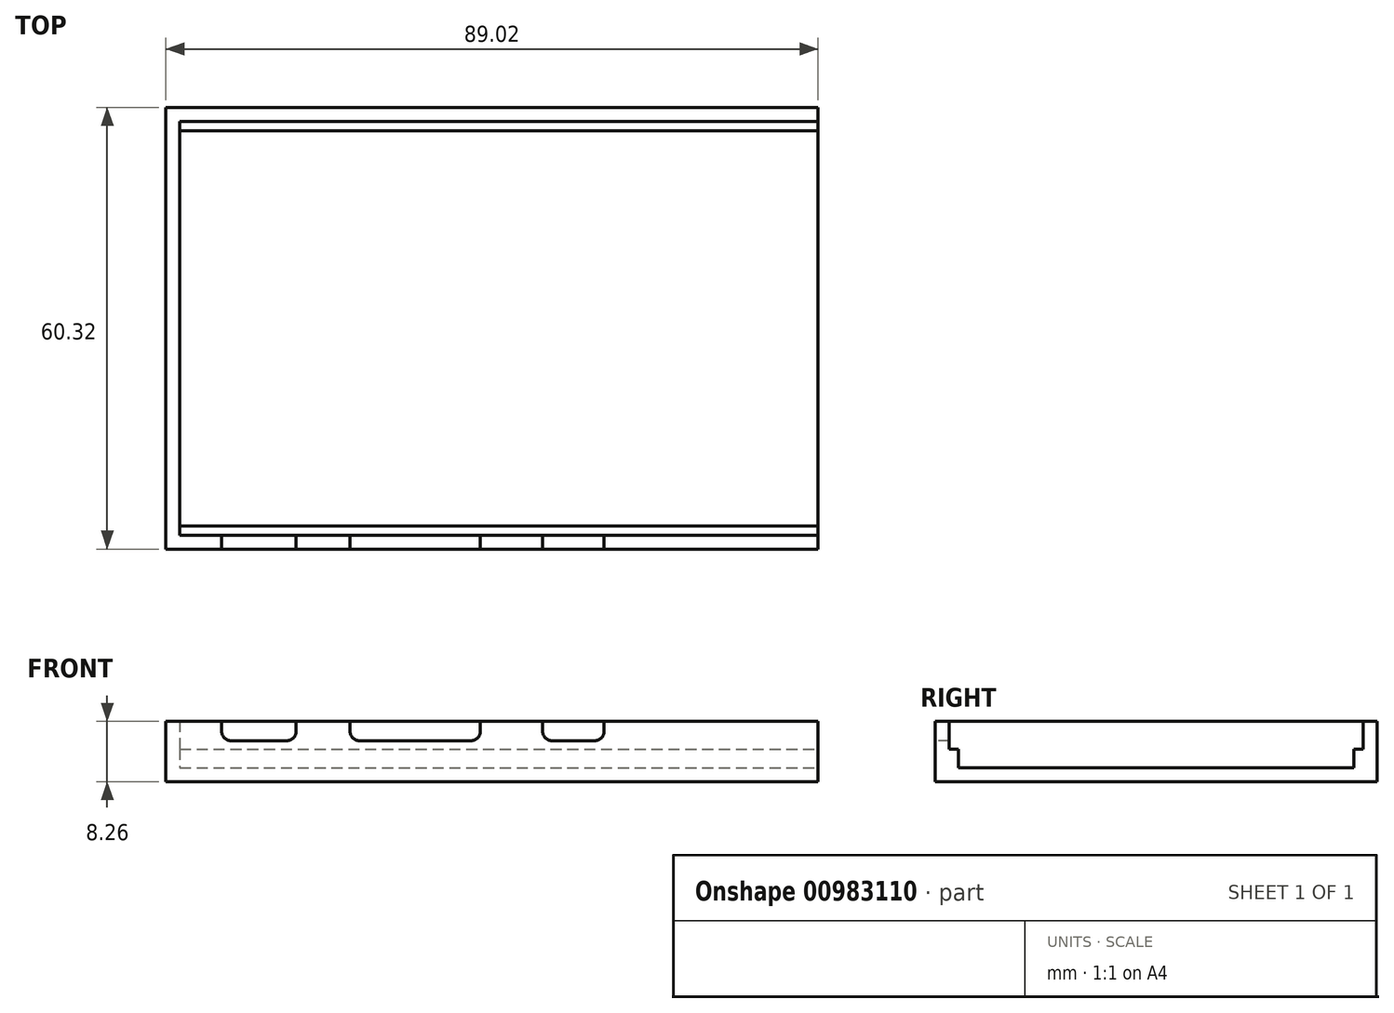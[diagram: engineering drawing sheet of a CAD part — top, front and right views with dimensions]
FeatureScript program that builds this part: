
annotation { "Feature Type Name" : "Feature", "Feature Type Description" : "" }
export const myFeature = defineFeature(function(context is Context, id is Id, definition is map)
    precondition{}
    {
        {
            var Q0;
            Q0=qCreatedBy(makeId("Top.planeOp"),FACE);
            var sketch = newSketch(context, id + "F0", { "sketchPlane" : qUnion([Q0])});
            skLineSegment(sketch, "E0.bottom", {"start": v(-44.45, -28.26) * mm, "end": v(44.45, -28.26) * mm, "construction": true});
            skLineSegment(sketch, "E0.top", {"start": v(-44.45, 28.26) * mm, "end": v(44.45, 28.26) * mm, "construction": true});
            skLineSegment(sketch, "E0.left", {"start": v(-44.45, -28.26) * mm, "end": v(-44.45, 28.26) * mm, "construction": true});
            skLineSegment(sketch, "E0.right", {"start": v(44.45, -28.26) * mm, "end": v(44.45, 28.26) * mm, "construction": true});
            skLineSegment(sketch, "E1", {"start": v(-44.45, -28.26) * mm, "end": v(44.45, 28.26) * mm, "construction": true});
            skLineSegment(sketch, "E2.bottom", {"start": v(-46.35, 30.16) * mm, "end": v(42.67, 30.16) * mm});
            skLineSegment(sketch, "E2.right", {"start": v(42.67, 30.16) * mm, "end": v(42.67, -30.16) * mm});
            skLineSegment(sketch, "E3", {"start": v(-52.76, 0) * mm, "end": v(63.48, 0) * mm, "construction": true});
            skLineSegment(sketch, "E4.MirrorCS", {"start": v(-46.35, -30.16) * mm, "end": v(42.67, -30.16) * mm});
            skLineSegment(sketch, "E5", {"start": v(-46.36, 30.16) * mm, "end": v(-46.35, -30.16) * mm});
            skSolve(sketch);
        }
        {
            var Q0;
            Q0 = qSketchRegion(id + "F0", true);
            extrude(context, id + "F1", {"entities" : qUnion([Q0]), "oppositeDirection" : true, "depth" : 1.9 * mm, "offsetDistance" : 25.4 * mm});
        }
        {
            var Q0;
            Q0=makeQuery(id+"F1.opExtrude","CAP_FACE",FACE,{"disambiguationData":[OSD([sQuery(id+"F0.wireOp",EDGE,"E2.bottom"),sQuery(id+"F0.wireOp",EDGE,"E2.right"),sQuery(id+"F0.wireOp",EDGE,"E4.MirrorCS"),sQuery(id+"F0.wireOp",EDGE,"E5")])],"isStart":true});
            var sketch = newSketch(context, id + "F2", { "sketchPlane" : qUnion([Q0])});
            skLineSegment(sketch, "E6.0", {"start": v(-44.45, 28.26) * mm, "end": v(42.67, 28.26) * mm});
            skLineSegment(sketch, "E6.1", {"start": v(-44.45, 28.26) * mm, "end": v(-44.45, -28.26) * mm});
            skLineSegment(sketch, "E6.2", {"start": v(-44.45, -28.26) * mm, "end": v(42.67, -28.26) * mm});
            skSolve(sketch);
        }
        {
            var Q0;
            Q0 = qSketchRegion(id + "F2", true);
            var Q1;
            {var subQ2=sQuery(id+"F2.wireOp",EDGE,"E6.0");Q1=makeQuery(id+"F2.imprint","IMPRINT",FACE,{"disambiguationData":[TD([[makeQuery(id+"F2.imprint","IMPRINT",EDGE,{"derivedFrom":subQ2}),1.0]])]});}
            extrude(context, id + "F3", {"entities" : qUnion([Q0, Q1]), "operationType" : NewBodyOperationType.ADD, "depth" : 6.35 * mm, "offsetDistance" : 25.4 * mm});
        }
        {
            var Q0;
            Q0=makeQuery(id+"F1.opExtrude","CAP_FACE",FACE,{"disambiguationData":[OSD([sQuery(id+"F0.wireOp",EDGE,"E2.bottom"),sQuery(id+"F0.wireOp",EDGE,"E2.right"),sQuery(id+"F0.wireOp",EDGE,"E4.MirrorCS"),sQuery(id+"F0.wireOp",EDGE,"E5")])],"isStart":true});
            var sketch = newSketch(context, id + "F4", { "sketchPlane" : qUnion([Q0])});
            skLineSegment(sketch, "E7", {"start": v(42.67, 0) * mm, "end": v(-44.45, 0) * mm, "construction": true});
            skLineSegment(sketch, "E8", {"start": v(-44.45, 26.99) * mm, "end": v(42.67, 26.99) * mm});
            skLineSegment(sketch, "E9.MirrorCS", {"start": v(-44.45, -26.99) * mm, "end": v(42.67, -26.99) * mm});
            skSolve(sketch);
        }
        {
            var Q0;
            Q0 = qSketchRegion(id + "F4", true);
            var Q1;
            {var subQ0=sQuery(id+"F4.wireOp",EDGE,"E8");Q1=makeQuery(id+"F4.imprint","IMPRINT",FACE,{"disambiguationData":[TD([[makeQuery(id+"F4.imprint","IMPRINT",EDGE,{"derivedFrom":subQ0}),1.0]])]});}
            var Q2;
            {var subQ0=sQuery(id+"F4.wireOp",EDGE,"E9.MirrorCS");Q2=makeQuery(id+"F4.imprint","IMPRINT",FACE,{"disambiguationData":[TD([[makeQuery(id+"F4.imprint","IMPRINT",EDGE,{"derivedFrom":subQ0}),-1.0]])]});}
            extrude(context, id + "F5", {"entities" : qUnion([Q0, Q1, Q2]), "operationType" : NewBodyOperationType.ADD, "depth" : 2.54 * mm, "offsetDistance" : 25.4 * mm});
        }
        {
            var Q0;
            {var subQ0=sQuery(id+"F0.wireOp",EDGE,"E4.MirrorCS");Q0=makeQuery(id+"F3.boolean.opBoolean","MERGE",FACE,{"derivedFrom":[makeQuery(id+"F1.opExtrude","SWEPT_FACE",FACE,{"disambiguationData":[OSD([subQ0])]}),makeQuery(id+"F3.opExtrude","SWEPT_FACE",FACE,{"disambiguationData":[OSD([subQ0])]})]});}
            var sketch = newSketch(context, id + "F6", { "sketchPlane" : qUnion([Q0])});
            skLineSegment(sketch, "E10", {"start": v(-38.73, 6.35) * mm, "end": v(-38.73, -1.9) * mm});
            skLineSegment(sketch, "E11", {"start": v(-38.73, -1.9) * mm, "end": v(-28.57, 6.35) * mm, "construction": true});
            skLineSegment(sketch, "E12", {"start": v(-28.57, 6.35) * mm, "end": v(-28.57, -1.9) * mm});
            skLineSegment(sketch, "E13", {"start": v(-21.2, 6.35) * mm, "end": v(-21.2, -1.9) * mm});
            skLineSegment(sketch, "E14", {"start": v(-21.2, -1.9) * mm, "end": v(-3.43, 6.35) * mm, "construction": true});
            skLineSegment(sketch, "E15", {"start": v(-3.43, 6.35) * mm, "end": v(-3.43, -1.9) * mm});
            skLineSegment(sketch, "E16", {"start": v(5.08, 6.35) * mm, "end": v(5.08, -1.9) * mm});
            skLineSegment(sketch, "E17", {"start": v(5.08, -1.9) * mm, "end": v(13.46, 6.35) * mm, "construction": true});
            skLineSegment(sketch, "E18", {"start": v(13.46, 6.35) * mm, "end": v(13.46, -1.9) * mm});
            skLineSegment(sketch, "E19", {"start": v(-46.35, 2.22) * mm, "end": v(13.46, 2.22) * mm, "construction": true});
            skPoint(sketch, "E20", {"position": v(-33.65, 2.22) * mm});
            skPoint(sketch, "E21", {"position": v(-12.32, 2.22) * mm});
            skPoint(sketch, "E22", {"position": v(9.27, 2.22) * mm});
            skLineSegment(sketch, "E23", {"start": v(-38.73, 3.68) * mm, "end": v(-28.57, 3.68) * mm});
            skLineSegment(sketch, "E24", {"start": v(-21.2, 3.68) * mm, "end": v(-3.43, 3.68) * mm});
            skLineSegment(sketch, "E25", {"start": v(5.08, 3.68) * mm, "end": v(13.46, 3.68) * mm});
            skSolve(sketch);
        }
        {
            var Q0;
            Q0 = qSketchRegion(id + "F6", true);
            var Q1;
            {var subQ3=sQuery(id+"F6.wireOp",EDGE,"E23");Q1=makeQuery(id+"F6.imprint","IMPRINT",FACE,{"disambiguationData":[TD([[makeQuery(id+"F6.imprint","IMPRINT",EDGE,{"derivedFrom":subQ3}),1.0]])]});}
            var Q2;
            {var subQ3=sQuery(id+"F6.wireOp",EDGE,"E24");Q2=makeQuery(id+"F6.imprint","IMPRINT",FACE,{"disambiguationData":[TD([[makeQuery(id+"F6.imprint","IMPRINT",EDGE,{"derivedFrom":subQ3}),1.0]])]});}
            var Q3;
            {var subQ3=sQuery(id+"F6.wireOp",EDGE,"E25");Q3=makeQuery(id+"F6.imprint","IMPRINT",FACE,{"disambiguationData":[TD([[makeQuery(id+"F6.imprint","IMPRINT",EDGE,{"derivedFrom":subQ3}),1.0]])]});}
            extrude(context, id + "F7", {"entities" : qUnion([Q0, Q1, Q2, Q3]), "operationType" : NewBodyOperationType.REMOVE, "oppositeDirection" : true, "depth" : 25.4 * mm, "offsetDistance" : 25.4 * mm});
        }
        {
            var Q0;
            Q0=makeQuery(id+"F7.boolean.opBoolean","COPY",EDGE,{"derivedFrom":makeQuery(id+"F7.opExtrude","SWEPT_EDGE",EDGE,{"disambiguationData":[OSD([sQuery(id+"F6.wireOp",EDGE,"E10"),sQuery(id+"F6.wireOp",EDGE,"E23")])]})});
            var Q1;
            Q1=makeQuery(id+"F7.boolean.opBoolean","COPY",EDGE,{"derivedFrom":makeQuery(id+"F7.opExtrude","SWEPT_EDGE",EDGE,{"disambiguationData":[OSD([sQuery(id+"F6.wireOp",EDGE,"E12"),sQuery(id+"F6.wireOp",EDGE,"E23")])]})});
            var Q2;
            Q2=makeQuery(id+"F7.boolean.opBoolean","COPY",EDGE,{"derivedFrom":makeQuery(id+"F7.opExtrude","SWEPT_EDGE",EDGE,{"disambiguationData":[OSD([sQuery(id+"F6.wireOp",EDGE,"E16"),sQuery(id+"F6.wireOp",EDGE,"E25")])]})});
            var Q3;
            Q3=makeQuery(id+"F7.boolean.opBoolean","COPY",EDGE,{"derivedFrom":makeQuery(id+"F7.opExtrude","SWEPT_EDGE",EDGE,{"disambiguationData":[OSD([sQuery(id+"F6.wireOp",EDGE,"E18"),sQuery(id+"F6.wireOp",EDGE,"E25")])]})});
            var Q4;
            Q4=makeQuery(id+"F7.boolean.opBoolean","COPY",EDGE,{"derivedFrom":makeQuery(id+"F7.opExtrude","SWEPT_EDGE",EDGE,{"disambiguationData":[OSD([sQuery(id+"F6.wireOp",EDGE,"E15"),sQuery(id+"F6.wireOp",EDGE,"E24")])]})});
            var Q5;
            Q5=makeQuery(id+"F7.boolean.opBoolean","COPY",EDGE,{"derivedFrom":makeQuery(id+"F7.opExtrude","SWEPT_EDGE",EDGE,{"disambiguationData":[OSD([sQuery(id+"F6.wireOp",EDGE,"E13"),sQuery(id+"F6.wireOp",EDGE,"E24")])]})});
            fillet(context, id + "F8", {"entities" : qUnion([Q0, Q1, Q2, Q3, Q4, Q5]), "radius" : 1.27 * mm, "tangentPropagation" : true, "allowEdgeOverflow" : false});
        }
    });
